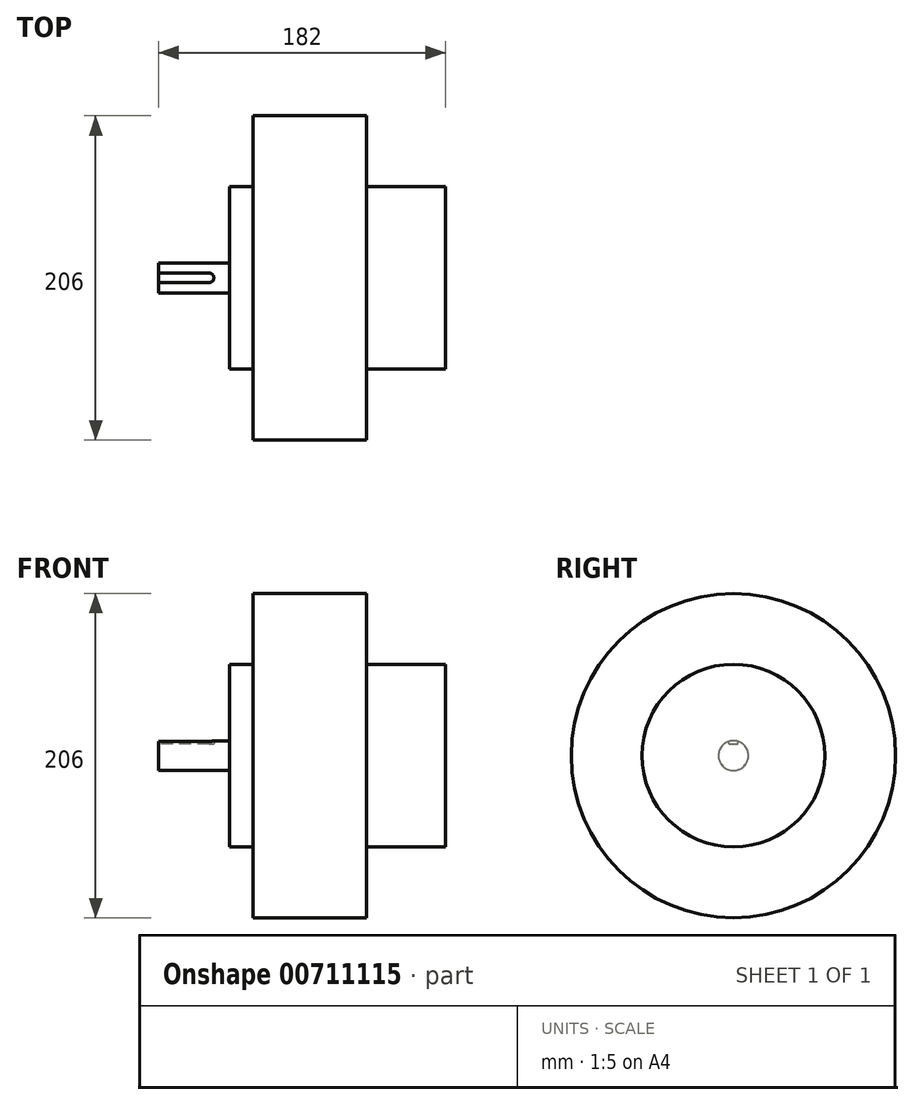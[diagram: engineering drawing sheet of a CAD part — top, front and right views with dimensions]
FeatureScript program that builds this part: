
annotation { "Feature Type Name" : "Feature", "Feature Type Description" : "" }
export const myFeature = defineFeature(function(context is Context, id is Id, definition is map)
    precondition{}
    {
        {
            var Q0;
            Q0=qCreatedBy(makeId("Right.planeOp"),FACE);
            var sketch = newSketch(context, id + "F0", { "sketchPlane" : qUnion([Q0])});
            skCircle(sketch, "E0", {"center": v(0, 0) * mm, "radius": 103 * mm});
            skSolve(sketch);
        }
        {
            var Q0;
            Q0=makeQuery(id+"F0.imprint","IMPRINT",FACE,{"disambiguationData":[TD([[makeQuery(id+"F0.imprint","IMPRINT",EDGE,{"derivedFrom":sQuery(id+"F0.wireOp",EDGE,"E0")}),1.0]])]});
            extrude(context, id + "F1", {"entities" : qUnion([Q0]), "endBound" : BoundingType.SYMMETRIC, "depth" : 72 * mm, "offsetDistance" : 25 * mm});
        }
        {
            var Q0;
            Q0=makeQuery(id+"F1.opExtrude","CAP_FACE",FACE,{"disambiguationData":[OSD([sQuery(id+"F0.wireOp",EDGE,"E0")])],"isStart":false});
            var sketch = newSketch(context, id + "F2", { "sketchPlane" : qUnion([Q0])});
            skCircle(sketch, "E1", {"center": v(0, 0) * mm, "radius": 58 * mm});
            skSolve(sketch);
        }
        {
            var Q0;
            Q0=makeQuery(id+"F2.imprint","IMPRINT",FACE,{"disambiguationData":[TD([[makeQuery(id+"F2.imprint","IMPRINT",EDGE,{"derivedFrom":sQuery(id+"F2.wireOp",EDGE,"E1")}),1.0]])]});
            extrude(context, id + "F3", {"entities" : qUnion([Q0]), "operationType" : NewBodyOperationType.ADD, "depth" : 50 * mm, "offsetDistance" : 25 * mm});
        }
        {
            var Q0;
            Q0=makeQuery(id+"F1.opExtrude","CAP_FACE",FACE,{"disambiguationData":[OSD([sQuery(id+"F0.wireOp",EDGE,"E0")])],"isStart":true});
            var sketch = newSketch(context, id + "F4", { "sketchPlane" : qUnion([Q0])});
            skCircle(sketch, "E2", {"center": v(0, 0) * mm, "radius": 58 * mm});
            skSolve(sketch);
        }
        {
            var Q0;
            Q0 = qSketchRegion(id + "F4", true);
            extrude(context, id + "F5", {"entities" : qUnion([Q0]), "operationType" : NewBodyOperationType.ADD, "depth" : 15 * mm, "offsetDistance" : 25 * mm});
        }
        {
            var Q0;
            Q0=makeQuery(id+"F5.opExtrude","CAP_FACE",FACE,{"disambiguationData":[OSD([sQuery(id+"F4.wireOp",EDGE,"E2")])],"isStart":false});
            var sketch = newSketch(context, id + "F6", { "sketchPlane" : qUnion([Q0])});
            skCircle(sketch, "E3", {"center": v(0, 0) * mm, "radius": 9.5 * mm});
            skSolve(sketch);
        }
        {
            var Q0;
            Q0 = qSketchRegion(id + "F6", true);
            extrude(context, id + "F7", {"entities" : qUnion([Q0]), "operationType" : NewBodyOperationType.ADD, "depth" : 45 * mm, "offsetDistance" : 25 * mm});
        }
        {
            var Q0;
            Q0=makeQuery(id+"F7.opExtrude","CAP_FACE",FACE,{"disambiguationData":[OSD([sQuery(id+"F6.wireOp",EDGE,"E3")])],"isStart":false});
            var sketch = newSketch(context, id + "F8", { "sketchPlane" : qUnion([Q0])});
            skLineSegment(sketch, "E4.bottom", {"start": v(3, 7.5) * mm, "end": v(-3, 7.5) * mm});
            skLineSegment(sketch, "E4.top", {"start": v(3, 11.5) * mm, "end": v(-3, 11.5) * mm});
            skLineSegment(sketch, "E4.left", {"start": v(3, 7.5) * mm, "end": v(3, 11.5) * mm});
            skLineSegment(sketch, "E4.right", {"start": v(-3, 7.5) * mm, "end": v(-3, 11.5) * mm});
            skPoint(sketch, "E4.middle", {"position": v(0, 9.5) * mm});
            skSolve(sketch);
        }
        {
            var Q0;
            Q0 = qSketchRegion(id + "F8", true);
            extrude(context, id + "F9", {"entities" : qUnion([Q0]), "operationType" : NewBodyOperationType.REMOVE, "oppositeDirection" : true, "depth" : 35 * mm, "offsetDistance" : 25 * mm});
        }
        {
            var Q0;
            Q0=makeQuery(id+"F9.boolean.opBoolean","COPY",EDGE,{"derivedFrom":makeQuery(id+"F9.opExtrude","CAP_EDGE",EDGE,{"disambiguationData":[OSD([sQuery(id+"F8.wireOp",EDGE,"E4.right")])],"isStart":false})});
            var Q1;
            Q1=makeQuery(id+"F9.boolean.opBoolean","COPY",EDGE,{"derivedFrom":makeQuery(id+"F9.opExtrude","CAP_EDGE",EDGE,{"disambiguationData":[OSD([sQuery(id+"F8.wireOp",EDGE,"E4.left")])],"isStart":false})});
            fillet(context, id + "F10", {"entities" : qUnion([Q0, Q1]), "radius" : 3 * mm, "tangentPropagation" : true, "allowEdgeOverflow" : false});
        }
    });
